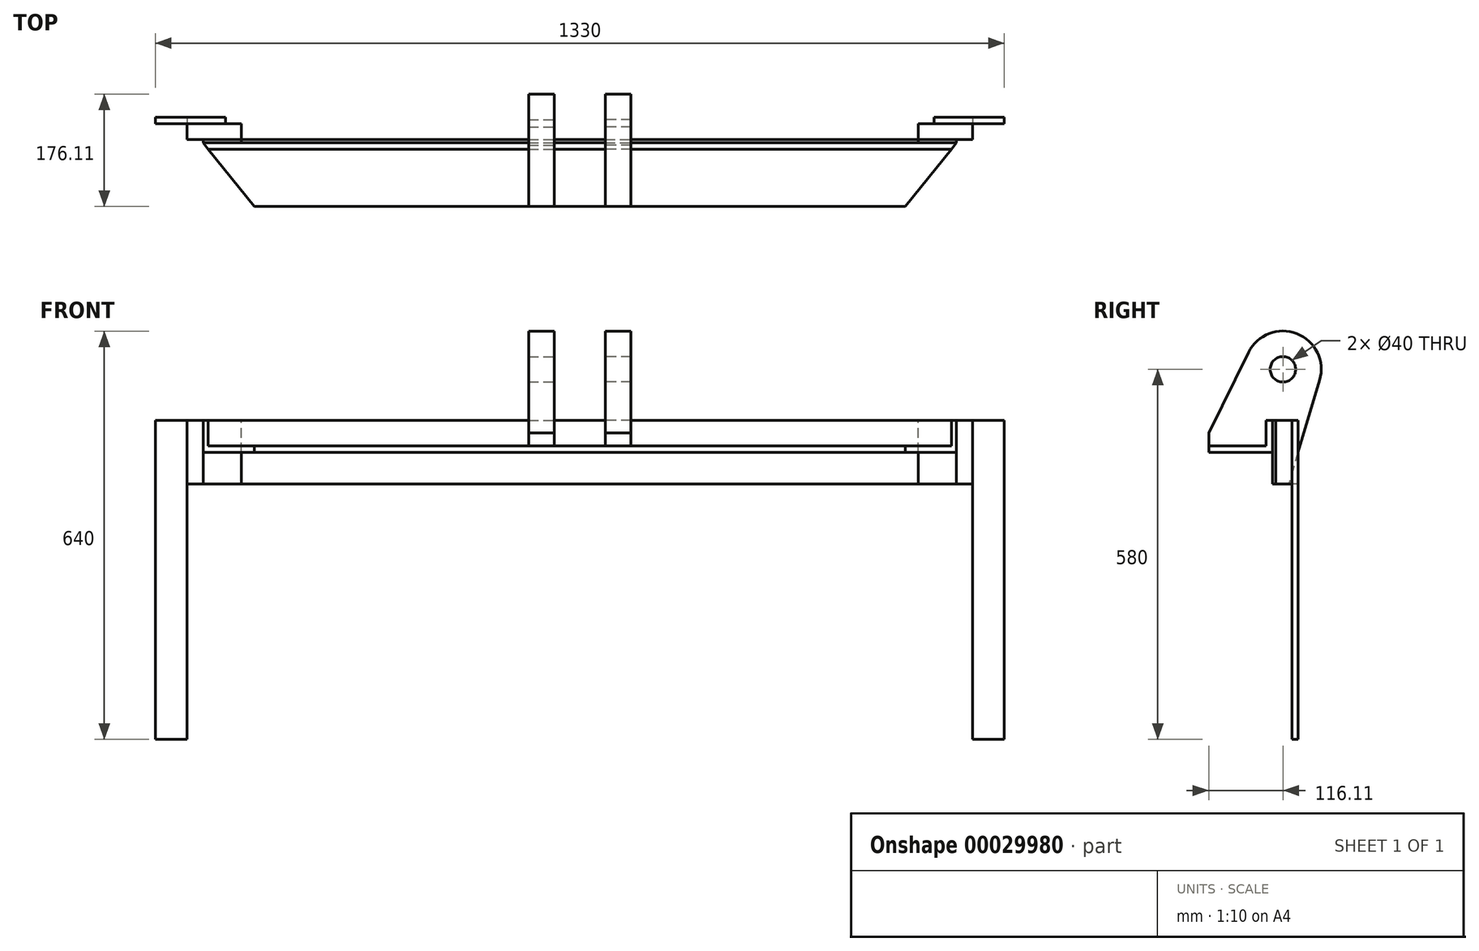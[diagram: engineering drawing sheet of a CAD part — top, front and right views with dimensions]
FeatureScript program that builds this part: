
annotation { "Feature Type Name" : "Feature", "Feature Type Description" : "" }
export const myFeature = defineFeature(function(context is Context, id is Id, definition is map)
    precondition{}
    {
        {
            var Q0;
            Q0=qCreatedBy(makeId("Front.planeOp"),FACE);
            var sketch = newSketch(context, id + "F0", { "sketchPlane" : qUnion([Q0])});
            skLineSegment(sketch, "E0", {"start": v(0, 440.97) * mm, "end": v(0, 0) * mm, "construction": true});
            skLineSegment(sketch, "E1", {"start": v(0, 0) * mm, "end": v(628.84, 0) * mm, "construction": true});
            skLineSegment(sketch, "E2", {"start": v(555, 0) * mm, "end": v(555, 100) * mm});
            skLineSegment(sketch, "E3", {"start": v(555, 100) * mm, "end": v(665, 100) * mm});
            skLineSegment(sketch, "E4", {"start": v(665, 100) * mm, "end": v(665, -400) * mm});
            skLineSegment(sketch, "E5", {"start": v(665, -400) * mm, "end": v(615, -400) * mm});
            skLineSegment(sketch, "E6", {"start": v(615, -400) * mm, "end": v(615, 0) * mm});
            skLineSegment(sketch, "E7", {"start": v(615, 0) * mm, "end": v(555, 0) * mm});
            skLineSegment(sketch, "E8.MirrorCS", {"start": v(-615, -400) * mm, "end": v(-615, 0) * mm});
            skLineSegment(sketch, "E9.MirrorCS", {"start": v(-615, 0) * mm, "end": v(-555, 0) * mm});
            skLineSegment(sketch, "E10.MirrorCS", {"start": v(-555, 0) * mm, "end": v(-555, 100) * mm});
            skLineSegment(sketch, "E11.MirrorCS", {"start": v(-555, 100) * mm, "end": v(-665, 100) * mm});
            skLineSegment(sketch, "E12.MirrorCS", {"start": v(-665, 100) * mm, "end": v(-665, -400) * mm});
            skLineSegment(sketch, "E13.MirrorCS", {"start": v(-665, -400) * mm, "end": v(-615, -400) * mm});
            skSolve(sketch);
        }
        {
            var Q0;
            Q0 = qSketchRegion(id + "F0", true);
            extrude(context, id + "F1", {"entities" : qUnion([Q0]), "oppositeDirection" : true, "depth" : 10 * mm});
        }
        {
            var Q0;
            Q0=makeQuery(id+"F1.opExtrude","CAP_FACE",FACE,{"disambiguationData":[OSD([sQuery(id+"F0.wireOp",EDGE,"E2"),sQuery(id+"F0.wireOp",EDGE,"E3"),sQuery(id+"F0.wireOp",EDGE,"E4"),sQuery(id+"F0.wireOp",EDGE,"E5"),sQuery(id+"F0.wireOp",EDGE,"E6"),sQuery(id+"F0.wireOp",EDGE,"E7")])],"isStart":true});
            var sketch = newSketch(context, id + "F2", { "sketchPlane" : qUnion([Q0])});
            skLineSegment(sketch, "E14.bottom", {"start": v(615, 100) * mm, "end": v(530, 100) * mm});
            skLineSegment(sketch, "E14.top", {"start": v(615, 0) * mm, "end": v(530, 0) * mm});
            skLineSegment(sketch, "E14.left", {"start": v(615, 100) * mm, "end": v(615, 0) * mm});
            skLineSegment(sketch, "E14.right", {"start": v(530, 100) * mm, "end": v(530, 0) * mm});
            skLineSegment(sketch, "E15", {"start": v(0, 0) * mm, "end": v(0, 558.55) * mm, "construction": true});
            skLineSegment(sketch, "E16.MirrorCS", {"start": v(-530, 100) * mm, "end": v(-530, 0) * mm});
            skLineSegment(sketch, "E17.MirrorCS", {"start": v(-615, 100) * mm, "end": v(-530, 100) * mm});
            skLineSegment(sketch, "E18.MirrorCS", {"start": v(-615, 100) * mm, "end": v(-615, 0) * mm});
            skLineSegment(sketch, "E19.MirrorCS", {"start": v(-615, 0) * mm, "end": v(-530, 0) * mm});
            skSolve(sketch);
        }
        {
            var Q0;
            Q0=makeQuery(id+"F2.imprint","IMPRINT",FACE,{"disambiguationData":[TD([[makeQuery(id+"F2.imprint","IMPRINT",EDGE,{"derivedFrom":sQuery(id+"F2.wireOp",EDGE,"E16.MirrorCS")}),-1.0]])]});
            var Q1;
            {var subQ1=sQuery(id+"F2.wireOp",EDGE,"E14.right");Q1=makeQuery(id+"F2.imprint","IMPRINT",FACE,{"disambiguationData":[TD([[makeQuery(id+"F2.imprint","IMPRINT",EDGE,{"derivedFrom":subQ1}),1.0]])]});}
            var Q2;
            {var subQ1=sQuery(id+"F2.wireOp",EDGE,"E14.left");Q2=makeQuery(id+"F2.imprint","IMPRINT",FACE,{"disambiguationData":[TD([[makeQuery(id+"F2.imprint","IMPRINT",EDGE,{"derivedFrom":subQ1}),-1.0]])]});}
            extrude(context, id + "F3", {"entities" : qUnion([Q0, Q1, Q2]), "depth" : 25 * mm});
        }
        {
            var Q0;
            Q0=makeQuery(id+"F3.opExtrude","SWEPT_FACE",FACE,{"disambiguationData":[OSD([sQuery(id+"F2.wireOp",EDGE,"E14.bottom")])]});
            var sketch = newSketch(context, id + "F4", { "sketchPlane" : qUnion([Q0])});
            skLineSegment(sketch, "E20.bottom", {"start": v(530, -25) * mm, "end": v(590, -25) * mm});
            skLineSegment(sketch, "E20.top", {"start": v(530, -30) * mm, "end": v(590, -30) * mm});
            skLineSegment(sketch, "E20.left", {"start": v(530, -25) * mm, "end": v(530, -30) * mm});
            skLineSegment(sketch, "E21.bottom", {"start": v(-590, -25) * mm, "end": v(-530, -25) * mm});
            skLineSegment(sketch, "E21.top", {"start": v(-590, -30) * mm, "end": v(-530, -30) * mm});
            skLineSegment(sketch, "E21.left", {"start": v(-590, -25) * mm, "end": v(-590, -30) * mm});
            skLineSegment(sketch, "E21.right", {"start": v(-530, -25) * mm, "end": v(-530, -30) * mm});
            skLineSegment(sketch, "E22", {"start": v(590, -25) * mm, "end": v(590, -30) * mm});
            skSolve(sketch);
        }
        {
            var Q0;
            Q0 = qSketchRegion(id + "F4", true);
            extrude(context, id + "F5", {"entities" : qUnion([Q0]), "oppositeDirection" : true, "depth" : 100 * mm});
        }
        {
            var Q0;
            Q0=makeQuery(id+"F5.opExtrude","SWEPT_FACE",FACE,{"disambiguationData":[OSD([sQuery(id+"F4.wireOp",EDGE,"E21.left")])]});
            var sketch = newSketch(context, id + "F6", { "sketchPlane" : qUnion([Q0])});
            skLineSegment(sketch, "E23", {"start": v(30, 100) * mm, "end": v(30, 50) * mm});
            skLineSegment(sketch, "E24", {"start": v(30, 50) * mm, "end": v(130, 50) * mm});
            skLineSegment(sketch, "E25.0", {"start": v(40, 60) * mm, "end": v(130, 60) * mm});
            skLineSegment(sketch, "E25.1", {"start": v(40, 100) * mm, "end": v(40, 60) * mm});
            skLineSegment(sketch, "E26", {"start": v(30, 100) * mm, "end": v(40, 100) * mm});
            skLineSegment(sketch, "E27", {"start": v(130, 50) * mm, "end": v(130, 60) * mm});
            skSolve(sketch);
        }
        {
            var Q0;
            Q0 = qSketchRegion(id + "F6", true);
            extrude(context, id + "F7", {"entities" : qUnion([Q0]), "oppositeDirection" : true, "depth" : 1180 * mm});
        }
        {
            var Q0;
            Q0=makeQuery(id+"F7.opExtrude","SWEPT_FACE",FACE,{"disambiguationData":[OSD([sQuery(id+"F6.wireOp",EDGE,"E26")])]});
            var sketch = newSketch(context, id + "F8", { "sketchPlane" : qUnion([Q0])});
            skLineSegment(sketch, "E28", {"start": v(-590, -130) * mm, "end": v(-590, -30) * mm});
            skLineSegment(sketch, "E29", {"start": v(590, -130) * mm, "end": v(590, -30) * mm});
            skLineSegment(sketch, "E30", {"start": v(0, 0) * mm, "end": v(0, 195.04) * mm, "construction": true});
            skLineSegment(sketch, "E31", {"start": v(-590, -30) * mm, "end": v(-510, -130) * mm});
            skLineSegment(sketch, "E32", {"start": v(-510, -130) * mm, "end": v(-590, -130) * mm});
            skLineSegment(sketch, "E33", {"start": v(590, -30) * mm, "end": v(510, -130) * mm});
            skLineSegment(sketch, "E34", {"start": v(510, -130) * mm, "end": v(590, -130) * mm});
            skSolve(sketch);
        }
        {
            var Q0;
            Q0 = qSketchRegion(id + "F8", true);
            extrude(context, id + "F9", {"entities" : qUnion([Q0]), "operationType" : NewBodyOperationType.REMOVE, "oppositeDirection" : true, "depth" : 100 * mm});
        }
        {
            var Q0;
            Q0=makeQuery(id+"F5.opExtrude","CAP_FACE",FACE,{"disambiguationData":[OSD([sQuery(id+"F4.wireOp",EDGE,"E21.bottom"),sQuery(id+"F4.wireOp",EDGE,"E21.top"),sQuery(id+"F4.wireOp",EDGE,"E21.left"),sQuery(id+"F4.wireOp",EDGE,"E21.right")])],"isStart":true});
            var sketch = newSketch(context, id + "F10", { "sketchPlane" : qUnion([Q0])});
            skLineSegment(sketch, "E35.bottom", {"start": v(-530, -25) * mm, "end": v(530, -25) * mm});
            skLineSegment(sketch, "E35.top", {"start": v(-530, -30) * mm, "end": v(530, -30) * mm});
            skLineSegment(sketch, "E35.left", {"start": v(-530, -25) * mm, "end": v(-530, -30) * mm});
            skLineSegment(sketch, "E35.right", {"start": v(530, -25) * mm, "end": v(530, -30) * mm});
            skSolve(sketch);
        }
        {
            var Q0;
            Q0 = qSketchRegion(id + "F10", true);
            extrude(context, id + "F11", {"entities" : qUnion([Q0]), "oppositeDirection" : true, "depth" : 100 * mm});
        }
        {
            var Q0;
            Q0=qCreatedBy(makeId("Right.planeOp"),FACE);
            var sketch = newSketch(context, id + "F12", { "sketchPlane" : qUnion([Q0])});
            skLineSegment(sketch, "E36", {"start": v(-130, 60) * mm, "end": v(-130, 80) * mm});
            skLineSegment(sketch, "E37", {"start": v(-130, 80) * mm, "end": v(-67.72, 206.5) * mm});
            skArc(sketch, "E38", {"start": v(43.6, 162.84) * mm, "mid": v(8.02, 235.86) * mm, "end": v(-67.72, 206.5) * mm});
            skLineSegment(sketch, "E39", {"start": v(43.6, 162.84) * mm, "end": v(-5, 0) * mm});
            skLineSegment(sketch, "E40", {"start": v(-5, 0) * mm, "end": v(-25, 0) * mm});
            skCircle(sketch, "E41", {"center": v(-13.89, 180) * mm, "radius": 20 * mm});
            skLineSegment(sketch, "E42", {"start": v(-25, 0) * mm, "end": v(-25, 100) * mm});
            skLineSegment(sketch, "E43", {"start": v(-25, 100) * mm, "end": v(-40, 100) * mm});
            skLineSegment(sketch, "E44", {"start": v(-40, 100) * mm, "end": v(-40, 60) * mm});
            skLineSegment(sketch, "E45", {"start": v(-40, 60) * mm, "end": v(-130, 60) * mm});
            skSolve(sketch);
        }
        {
            var Q0;
            Q0=qCreatedBy(makeId("Right.planeOp"),FACE);
            cPlane(context, id + "F13", {"entities" : qUnion([Q0]), "cplaneType" : CPlaneType.OFFSET, "offset" : 40 * mm, "oppositeDirection" : true, "width" : 150 * mm, "height" : 150 * mm});
        }
        {
            var Q0;
            Q0=qCreatedBy(id+"F13.planeOp",FACE);
            var sketch = newSketch(context, id + "F14", { "sketchPlane" : qUnion([Q0])});
            skLineSegment(sketch, "E46.0", {"start": v(43.6, 162.84) * mm, "end": v(-5, 0) * mm});
            skLineSegment(sketch, "E47.0", {"start": v(-5, 0) * mm, "end": v(-25, 0) * mm});
            skLineSegment(sketch, "E48.0", {"start": v(-25, 0) * mm, "end": v(-25, 100) * mm});
            skLineSegment(sketch, "E49.0", {"start": v(-25, 100) * mm, "end": v(-40, 100) * mm});
            skLineSegment(sketch, "E50.0", {"start": v(-40, 100) * mm, "end": v(-40, 60) * mm});
            skLineSegment(sketch, "E51.0", {"start": v(-40, 60) * mm, "end": v(-130, 60) * mm});
            skLineSegment(sketch, "E52.0", {"start": v(-130, 60) * mm, "end": v(-130, 80) * mm});
            skLineSegment(sketch, "E53.0", {"start": v(-130, 80) * mm, "end": v(-67.72, 206.5) * mm});
            skArc(sketch, "E54.0", {"start": v(43.6, 162.84) * mm, "mid": v(8.02, 235.86) * mm, "end": v(-67.72, 206.5) * mm});
            skCircle(sketch, "E55.0", {"center": v(-13.89, 180) * mm, "radius": 20 * mm});
            skSolve(sketch);
        }
        {
            var Q0;
            Q0=makeQuery(id+"F14.imprint","IMPRINT",FACE,{"disambiguationData":[TD([[makeQuery(id+"F14.imprint","IMPRINT",EDGE,{"derivedFrom":sQuery(id+"F14.wireOp",EDGE,"E46.0")}),-1.0]])]});
            extrude(context, id + "F15", {"entities" : qUnion([Q0]), "oppositeDirection" : true, "depth" : 40 * mm});
        }
        {
            var Q0;
            Q0=makeQuery(id+"F15.opExtrude","SWEPT_BODY",BODY,{"disambiguationData":[OSD([sQuery(id+"F14.wireOp",EDGE,"E46.0"),sQuery(id+"F14.wireOp",EDGE,"E47.0"),sQuery(id+"F14.wireOp",EDGE,"E48.0"),sQuery(id+"F14.wireOp",EDGE,"E49.0"),sQuery(id+"F14.wireOp",EDGE,"E50.0"),sQuery(id+"F14.wireOp",EDGE,"E51.0"),sQuery(id+"F14.wireOp",EDGE,"E52.0"),sQuery(id+"F14.wireOp",EDGE,"E53.0"),sQuery(id+"F14.wireOp",EDGE,"E54.0"),sQuery(id+"F14.wireOp",EDGE,"E55.0")])]});
            var Q1;
            Q1=qCreatedBy(makeId("Right.planeOp"),FACE);
            mirror(context, id + "F16", {"entities" : qUnion([Q0]), "mirrorPlane" : qUnion([Q1])});
        }
    });
